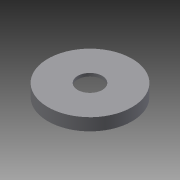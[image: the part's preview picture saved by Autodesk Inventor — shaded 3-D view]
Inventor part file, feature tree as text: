
AUTODESK INVENTOR PART (.ipt)
format: ipt  version: 2013 SP2 (Build 170200200, 200)  size: 85,504 bytes
history: native  units: mm
features: extrude x2, sketch x1
ambient origin geometry x8: Origin, YZ Plane, XZ Plane, XY Plane, X Axis, Y Axis, Z Axis, Center Point
bodies: Solid1 (feature_tree)
feature tree (3):
  sketch  "Sketch1"  dims[d0=4.0mm d1=8.4mm d2=13.7mm d3=2.0mm d4=0.0mm d5=1.5mm d6=0.0mm]
  extrude  "Extrusion1"  Depth=8.4mm
  extrude  "Extrusion2"  Depth=13.7mm
